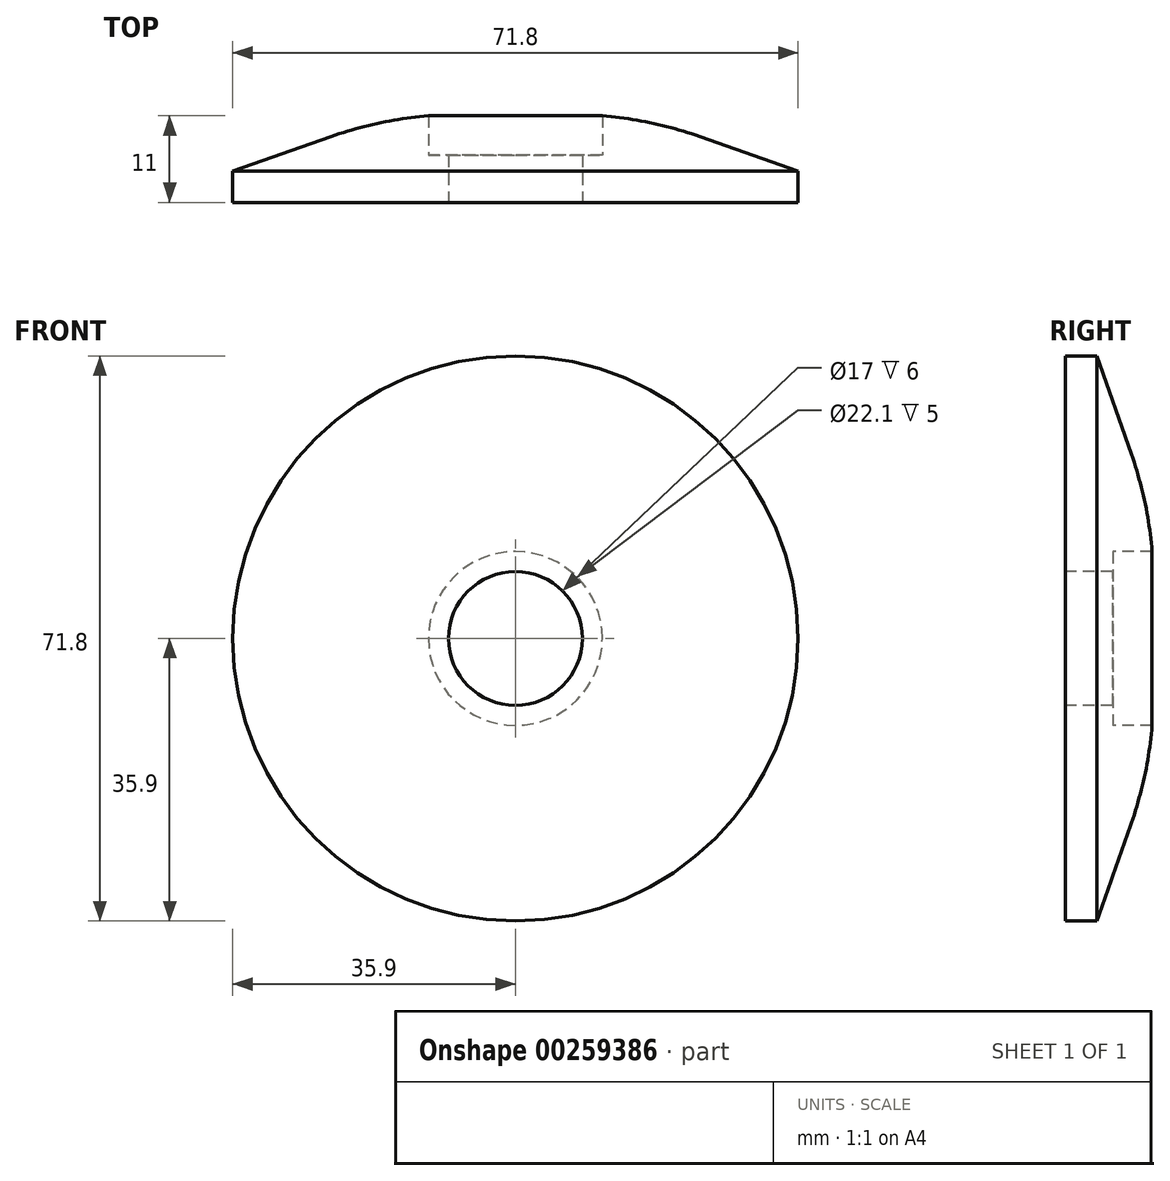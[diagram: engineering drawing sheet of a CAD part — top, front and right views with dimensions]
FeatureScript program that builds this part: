
annotation { "Feature Type Name" : "Feature", "Feature Type Description" : "" }
export const myFeature = defineFeature(function(context is Context, id is Id, definition is map)
    precondition{}
    {
        {
            var Q0;
            Q0=qCreatedBy(makeId("Front.planeOp"),FACE);
            var sketch = newSketch(context, id + "F0", { "sketchPlane" : qUnion([Q0])});
            skCircle(sketch, "E0", {"center": v(0, 0) * mm, "radius": 8.5 * mm});
            skCircle(sketch, "E1.0.0", {"center": v(0, 0) * mm, "radius": 35.9 * mm});
            skSolve(sketch);
        }
        {
            var Q0;
            Q0 = qSketchRegion(id + "F0", true);
            extrude(context, id + "F1", {"entities" : qUnion([Q0]), "oppositeDirection" : true, "depth" : 6 * mm});
        }
        {
            var Q0;
            Q0=makeQuery(id+"F1.opExtrude","CAP_FACE",FACE,{"disambiguationData":[OSD([sQuery(id+"F0.wireOp",EDGE,"E0"),sQuery(id+"F0.wireOp",EDGE,"1428627e-217f-4440-8e25-80f22d957af0.0")])],"isStart":false});
            var sketch = newSketch(context, id + "F2", { "sketchPlane" : qUnion([Q0])});
            skCircle(sketch, "E2", {"center": v(0, 0) * mm, "radius": 11.05 * mm});
            skCircle(sketch, "E3.0", {"center": v(0, 0) * mm, "radius": 35.9 * mm});
            skSolve(sketch);
        }
        {
            var Q0;
            Q0 = qSketchRegion(id + "F2", true);
            extrude(context, id + "F3", {"entities" : qUnion([Q0]), "operationType" : NewBodyOperationType.ADD, "depth" : 5 * mm});
        }
        {
            var Q0;
            Q0=makeQuery(id+"F3.opExtrude","CAP_EDGE",EDGE,{"disambiguationData":[OSD([sQuery(id+"F2.wireOp",EDGE,"ec30d4a8-2cc4-408f-80b0-493b41a83411.0.0")])],"isStart":false});
            var Q1;
            Q1=makeQuery(id+"F3.opExtrude","CAP_EDGE",EDGE,{"disambiguationData":[OSD([sQuery(id+"F2.wireOp",EDGE,"E3.0")])],"isStart":false});
            chamfer(context, id + "F4", {"entities" : qUnion([Q0, Q1]), "chamferType" : ChamferType.TWO_OFFSETS, "width1" : 7 * mm, "oppositeDirection" : false, "width2" : 20 * mm, "tangentPropagation" : true});
        }
        {
            var Q0;
            {var subQ0=sQuery(id+"F2.wireOp",EDGE,"ec30d4a8-2cc4-408f-80b0-493b41a83411.0.0");Q0=makeQuery(id+"F4.opChamfer","BLEND_EDGE",EDGE,{"blendedFrom":[makeQuery(id+"F3.opExtrude","CAP_EDGE",EDGE,{"disambiguationData":[OSD([subQ0])],"isStart":false}),makeQuery(id+"F3.opExtrude","CAP_FACE",FACE,{"disambiguationData":[OSD([sQuery(id+"F2.wireOp",EDGE,"E2"),subQ0])],"isStart":false})],"blendedInto":[makeQuery(id+"F3.opExtrude","CAP_FACE",FACE,{"disambiguationData":[OSD([sQuery(id+"F2.wireOp",EDGE,"E2"),subQ0])],"isStart":false})]});}
            var Q1;
            {var subQ0=sQuery(id+"F2.wireOp",EDGE,"E3.0");Q1=makeQuery(id+"F4.opChamfer","BLEND_EDGE",EDGE,{"blendedFrom":[makeQuery(id+"F3.opExtrude","CAP_EDGE",EDGE,{"disambiguationData":[OSD([subQ0])],"isStart":false}),makeQuery(id+"F3.opExtrude","CAP_FACE",FACE,{"disambiguationData":[OSD([sQuery(id+"F2.wireOp",EDGE,"E2"),subQ0])],"isStart":false})],"blendedInto":[makeQuery(id+"F3.opExtrude","CAP_FACE",FACE,{"disambiguationData":[OSD([sQuery(id+"F2.wireOp",EDGE,"E2"),subQ0])],"isStart":false})]});}
            fillet(context, id + "F5", {"entities" : qUnion([Q0, Q1]), "radius" : 50 * mm, "tangentPropagation" : true, "allowEdgeOverflow" : false});
        }
    });
